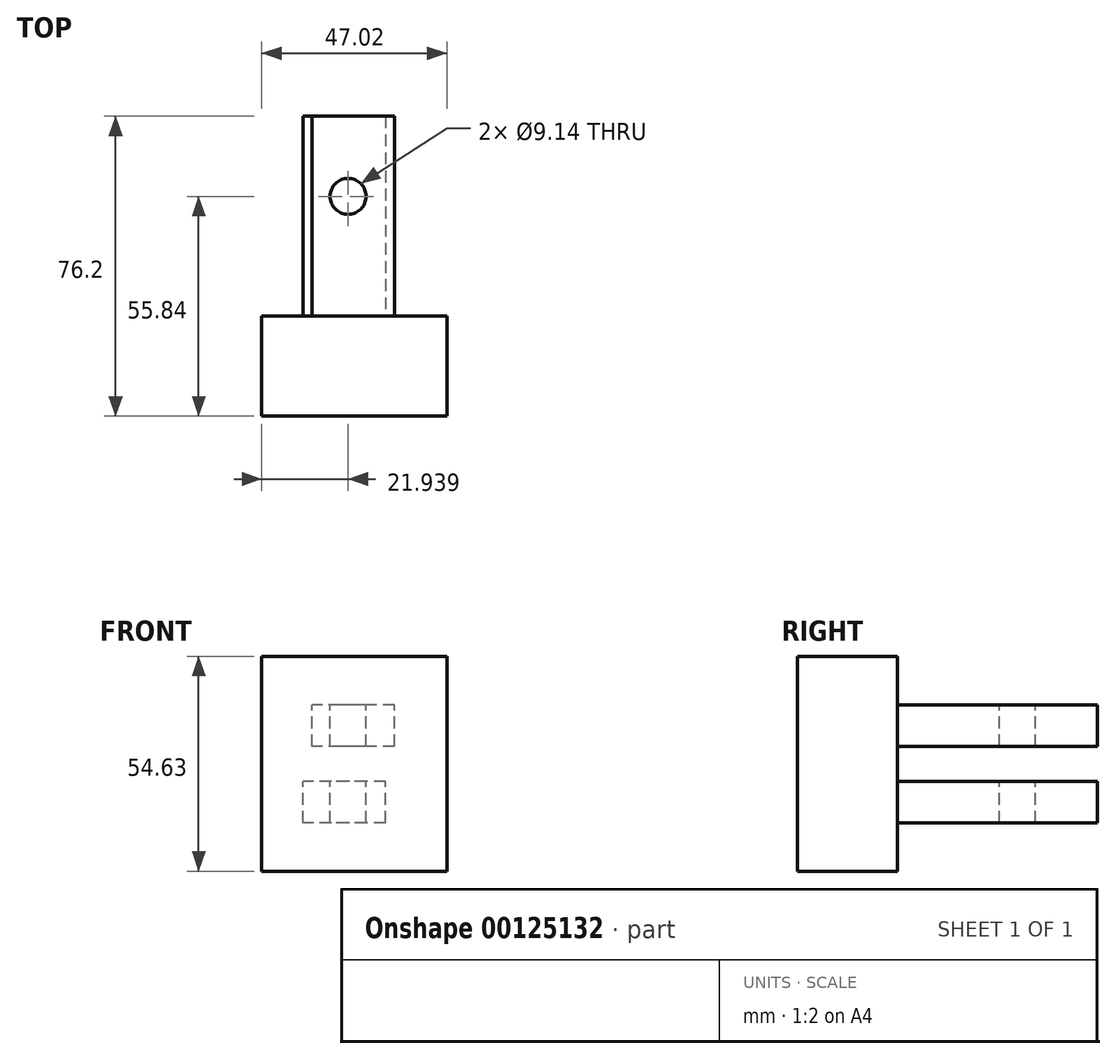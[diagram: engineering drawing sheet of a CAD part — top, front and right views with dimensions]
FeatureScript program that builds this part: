
annotation { "Feature Type Name" : "Feature", "Feature Type Description" : "" }
export const myFeature = defineFeature(function(context is Context, id is Id, definition is map)
    precondition{}
    {
        {
            var Q0;
            Q0=qCreatedBy(makeId("Front.planeOp"),FACE);
            var sketch = newSketch(context, id + "F0", { "sketchPlane" : qUnion([Q0])});
            skLineSegment(sketch, "E0.bottom", {"start": v(0, 0) * mm, "end": v(47.02, 0) * mm});
            skLineSegment(sketch, "E0.top", {"start": v(0, 54.63) * mm, "end": v(47.02, 54.63) * mm});
            skLineSegment(sketch, "E0.left", {"start": v(0, 0) * mm, "end": v(0, 54.63) * mm});
            skLineSegment(sketch, "E0.right", {"start": v(47.02, 0) * mm, "end": v(47.02, 54.63) * mm});
            skSolve(sketch);
        }
        {
            var Q0;
            Q0 = qSketchRegion(id + "F0", true);
            extrude(context, id + "F1", {"entities" : qUnion([Q0]), "depth" : 25.4 * mm});
        }
        {
            var Q0;
            Q0=makeQuery(id+"F1.opExtrude","CAP_FACE",FACE,{"disambiguationData":[OSD([sQuery(id+"F0.wireOp",EDGE,"E0.bottom"),sQuery(id+"F0.wireOp",EDGE,"E0.top"),sQuery(id+"F0.wireOp",EDGE,"E0.left"),sQuery(id+"F0.wireOp",EDGE,"E0.right")])],"isStart":true});
            var sketch = newSketch(context, id + "F2", { "sketchPlane" : qUnion([Q0])});
            skLineSegment(sketch, "E1.bottom", {"start": v(-33.78, 31.7) * mm, "end": v(-12.82, 31.7) * mm});
            skLineSegment(sketch, "E1.top", {"start": v(-33.78, 42.27) * mm, "end": v(-12.82, 42.27) * mm});
            skLineSegment(sketch, "E1.left", {"start": v(-33.78, 31.7) * mm, "end": v(-33.78, 42.27) * mm});
            skLineSegment(sketch, "E1.right", {"start": v(-12.82, 31.7) * mm, "end": v(-12.82, 42.27) * mm});
            skLineSegment(sketch, "E2.bottom", {"start": v(-31.5, 12.29) * mm, "end": v(-10.55, 12.29) * mm});
            skLineSegment(sketch, "E2.top", {"start": v(-31.5, 22.85) * mm, "end": v(-10.55, 22.85) * mm});
            skLineSegment(sketch, "E2.left", {"start": v(-31.5, 12.29) * mm, "end": v(-31.5, 22.85) * mm});
            skLineSegment(sketch, "E2.right", {"start": v(-10.55, 12.29) * mm, "end": v(-10.55, 22.85) * mm});
            skSolve(sketch);
        }
        {
            var Q0;
            Q0 = qSketchRegion(id + "F2", true);
            extrude(context, id + "F3", {"entities" : qUnion([Q0]), "operationType" : NewBodyOperationType.ADD, "depth" : 50.8 * mm});
        }
        {
            var Q0;
            Q0=makeQuery(id+"F3.opExtrude","SWEPT_FACE",FACE,{"disambiguationData":[OSD([sQuery(id+"F2.wireOp",EDGE,"E1.top")])]});
            var sketch = newSketch(context, id + "F4", { "sketchPlane" : qUnion([Q0])});
            skCircle(sketch, "E3", {"center": v(21.94, 30.44) * mm, "radius": 4.57 * mm});
            skSolve(sketch);
        }
        {
            var Q0;
            Q0 = qSketchRegion(id + "F4", true);
            extrude(context, id + "F5", {"entities" : qUnion([Q0]), "operationType" : NewBodyOperationType.REMOVE, "endBound" : BoundingType.THROUGH_ALL, "oppositeDirection" : true, "depth" : 254 * mm});
        }
    });
